# Revit family: spot_5.4
name_source: partatom
category: Lighting Fixtures
units: mm (PartAtom-declared; Revit-internal decimal feet)

## family parameters
Always vertical = No
Cut with Voids When Loaded = No
Light Source = No
OmniClass Number = 23.80.70.00
OmniClass Title = Lighting
Part Type = Normal
Room Calculation Point = No
Round Connector Dimension = Use Diameter
Shared = No
Work Plane-Based = Yes

## types (6) — shared parameters
Apparent Load = 52 VA
CCT = 3000 K
CRI = CRI80
Default Elevation = 1219 mm
Description = Outdoor Projectors
IK = IK10
IP = IP66
Lamp = LED
Manufacturer = L&L Luce&Light srl
Model = CF54
Rated Power supply = 230 V
URL = https://www.lucelight.it
Wattage = 52 W
Weight = 6.00 kg

## per-type parameters (varying)
| type | Lumen Output | Photometry |
| S 15° 52W | 3804 lm | CF54 Light source : S 15° 52W |
| M 25° 52W | 4908 lm | CF54 Light source : M 25° 52W |
| L 34° 52W | 5025 lm | CF54 Light source : L 34° 52W |
| J 53° 52W | 4412 lm | CF54 Light source : J 53° 52W |
| W 14°x65° 52W | 3274 lm | CF54 Light source : W 14°x65° 52W |
| X 22°x66° 52W | 4773 lm | CF54 Light source : X 22°x66° 52W |

## geometry (parser evidence)
native form markers: Sweep x4
no freeform markers — native parametric forms only
